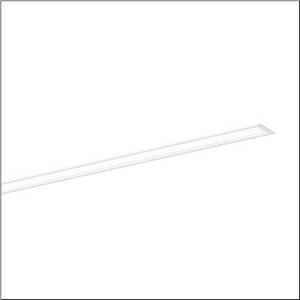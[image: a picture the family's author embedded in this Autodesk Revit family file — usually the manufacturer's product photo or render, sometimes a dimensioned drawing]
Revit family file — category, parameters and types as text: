
# Revit family: silica_r__21_51mx13tat4w_7811
name_source: partatom
category: Lighting Fixtures
units: mm (PartAtom-declared; Revit-internal decimal feet)

## family parameters
Cut with Voids When Loaded = No
Host = Face
Light Source = No
Part Type = Normal
Room Calculation Point = No
Round Connector Dimension = Use Diameter
Shared = No

## types (1)
- --- (1 x LED, 3230 lm, 32.4 W, 6500K)
    Apparent Load = 32 VA
    CIE Flux Codes = 78 96 99 100 100
    Color Rendering = 80
    Color Temperature = 6500K
    Default Elevation = 1800 mm
    Description = Silica® 21, office luminaire, primary optical cover: prismatic diffuser, of PMMA, CAT 2 (L<= 3000cd/m²), light emission: direct distribution, primary light characteristic: symmetric, installation type: recessed, LED, rated luminous flux: 3.230lm, luminous efficacy: 95lm/W, light colour: 8tw, colour temperature: 2700..6500K, control gear: DALI DT8, with terminal, 3+2-pole, max. 2.5mm², mains connection: 220..240V, AC, 50/60Hz, rated input power: 34W, luminaire housing, of aluminium, traffic white (RAL 9016), length: 1.228mm, width: 79mm, height: 53mm, protection rating (complete): IP20, insulation class (complete): insulation class I (protective earthing), certification: CE, ENEC, VDE, permissible operating ambient temperature: 0..+35°C, standard: EN 50419, packaging unit: 1 piece
    Height = 0 mm  [stored 0 ft]
    Lamp = 1 x LED
    Lamp Light Flux = 3230 lm
    Lamp Power = 32.4 W
    Lamp count = 1
    Length = 1227 mm
    Luminous efficacy = 100 lm/W
    Manufacturer = Siteco
    ModVariant = No
    Model = 51MX13TAT4W
    Mounting Place = Ceiling
    Mounting Type = Recessed
    Number of Poles = 1
    OnlyDefault = Yes
    Power Factor = 1
    Product Name = Silica® 21
    Product group = office luminaire | ceiling recessed
    ProductGroupID = 401
    Protection Class = Protection class I
    Protection Degree = IP 20
    RLX_Detail_Level = 1
    RLX_Emergency_Light_Flux = 0 lm
    RLX_Emergency_Type = 0
    RLX_Emergency_Type_DB = No
    RlxData = <blob elided: 13085 chars, md5=4b77aff9>
    Socket = socket
    Standby Power = 0 W
    System Light Flux = 3230 lm
    System Power = 32 W
    Type Comments = individual setting
    Type Image = l_1335881.jpg
    URL = http://relux.com
    VarID = @adj_139854
    Voltage = 0 V
    Weight = 0.00 kg
    Width = 79 mm

note: [stored X ft] marks values corroborated as IEEE doubles in the binary element streams (Revit-internal decimal feet)

## geometry (parser evidence)
native form markers: Sweep x9
no freeform markers — native parametric forms only
